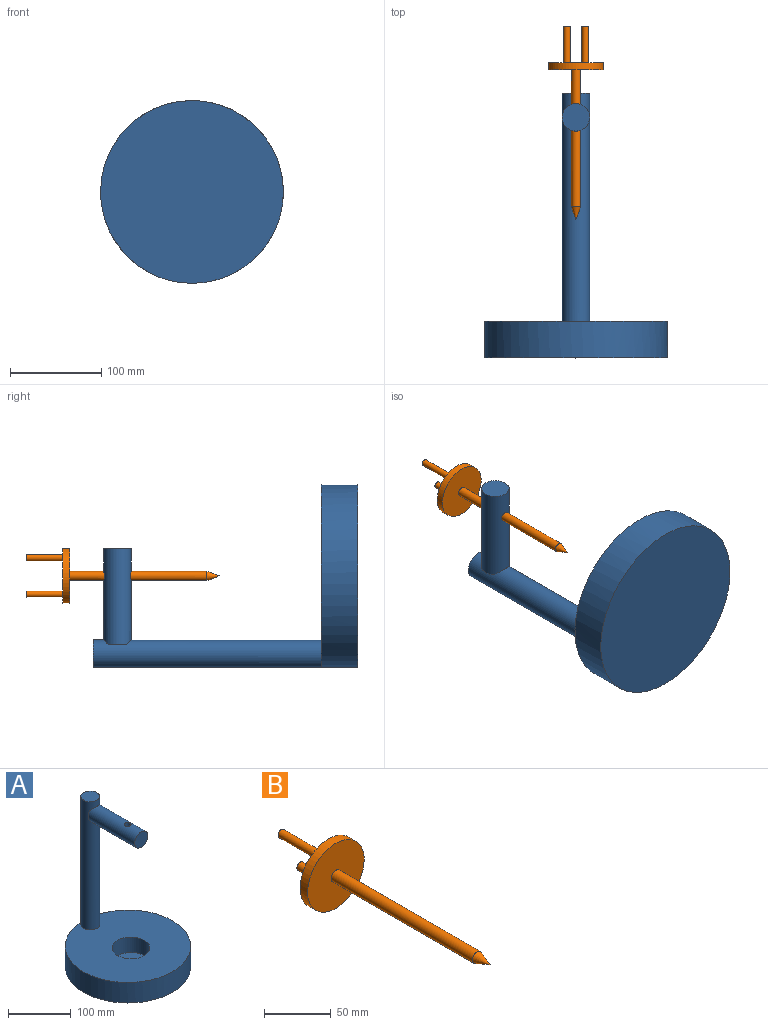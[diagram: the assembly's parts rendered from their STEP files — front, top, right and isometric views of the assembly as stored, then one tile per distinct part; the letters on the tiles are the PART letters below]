
ASSEMBLY  parts=2 mates=1
PART A: 12 faces, bbox 200x200x290 mm
  f0: cylinder r=15mm len=250mm, axis (0,0,-1), area 22891.1mm2, adj f2,f6,f7,f8,f9
  f1: cylinder r=100mm len=200mm, axis (0,0,-1), area 25132.7mm2, adj f2,f3
  f2: plane 200x200mm, normal (0,0,1), area 27881.6mm2, adj f0,f1,f4
  f3: plane 200x200mm, normal (0,0,-1), area 31415.9mm2, adj f1
  f4: cylinder r=30mm len=60mm, axis (0,0,1), area 5654.9mm2, adj f2,f5
  f5: plane 60x60mm, normal (0,0,1), area 2827.4mm2, adj f4
  f6: plane 30x30mm, normal (0,0,1), area 706.9mm2, adj f0
  f7: cylinder r=15mm len=105mm, axis (0,1,0), area 9563.6mm2, adj f0,f8,f9,f10,f11
  f8: plane 20x3.82mm, normal (0,1,0), area 52.4mm2, adj f0,f7
  f9: plane 20x3.82mm, normal (0,1,0), area 52.4mm2, adj f0,f7
  f10: plane 30x30mm, normal (0,-1,0), area 706.9mm2, adj f7
  f11: cylinder r=5.1mm len=30mm, axis (0,0,1), area 932.9mm2, adj f7
PART B: 9 faces, bbox 60x211.7x60 mm
  f0: cylinder r=5mm len=150mm, axis (0,1,0), area 4712.4mm2, adj f1,f4
  f1: cone r=5mm half-angle=20deg, axis (0,1,0), area 229.6mm2, adj f0
  f2: cylinder r=30mm len=60mm, axis (0,-1,0), area 1508mm2, adj f3,f4
  f3: plane 60x60mm, normal (0,1,0), area 2750.5mm2, adj f2,f5,f7
  f4: plane 60x60mm, normal (0,-1,0), area 2748.9mm2, adj f0,f2
  f5: cylinder r=3.5mm len=40mm, axis (0,-1,0), area 879.6mm2, adj f3,f6
  f6: plane 7x7mm, normal (0,1,0), area 38.5mm2, adj f5
  f7: cylinder r=3.5mm len=40mm, axis (0,-1,0), area 879.6mm2, adj f3,f8
  f8: plane 7x7mm, normal (0,1,0), area 38.5mm2, adj f7
PLACE A rot(axis=(-1,0,0),90deg) t=(-182.94,-53.08,250.22)mm
PLACE B t=(-182.94,262.17,250.22)mm
MATE slider B.f0 <-> A.f11  axis (0,1,0) through (-182.94,187.17,250.22)mm
